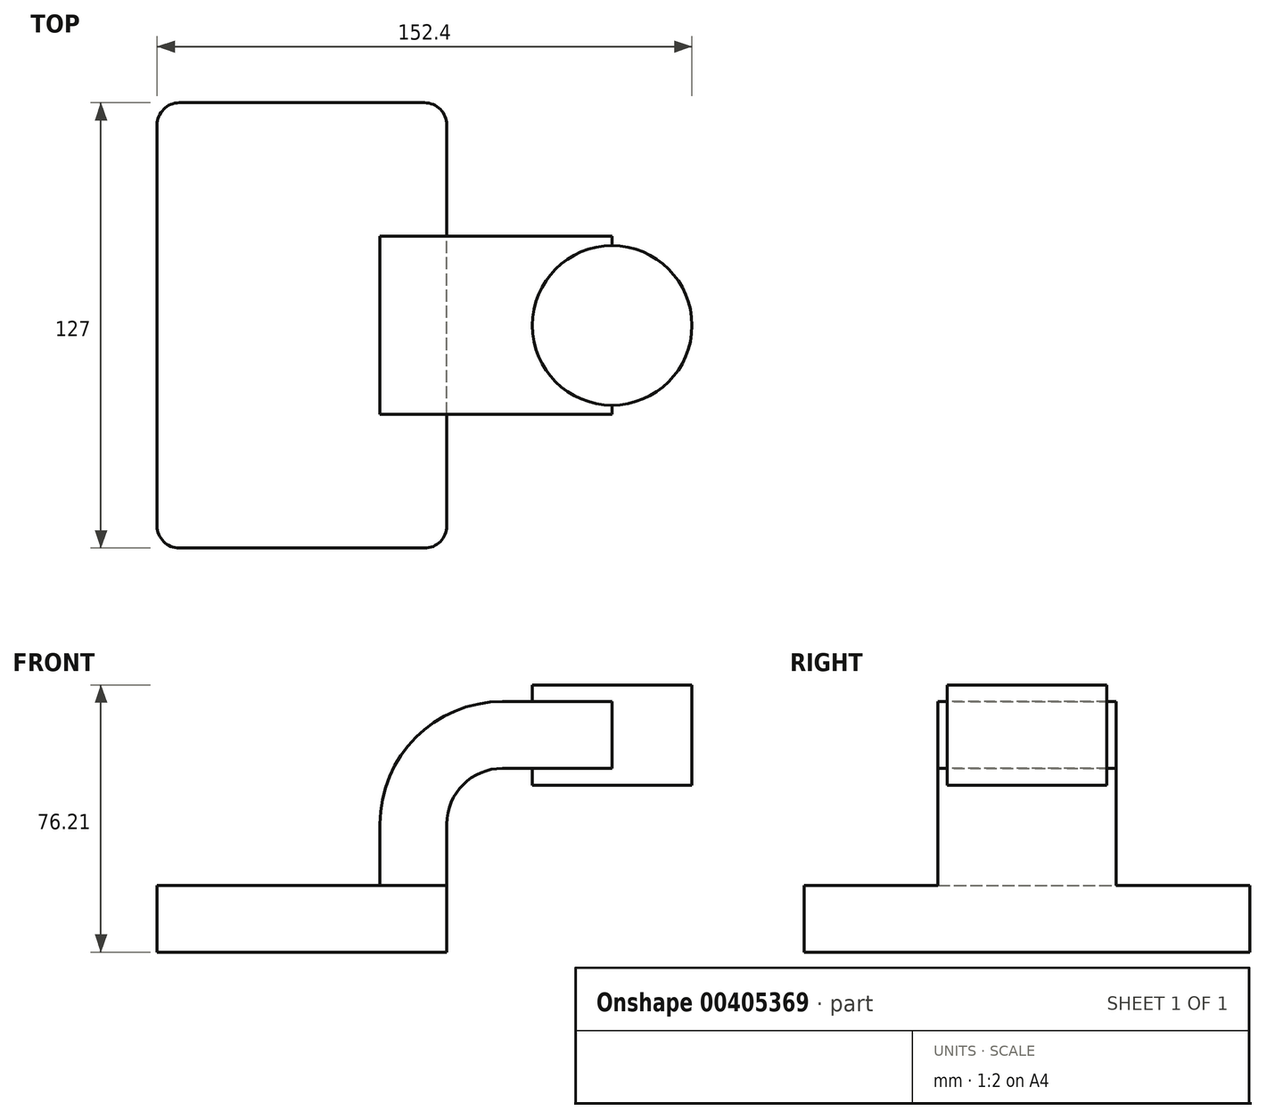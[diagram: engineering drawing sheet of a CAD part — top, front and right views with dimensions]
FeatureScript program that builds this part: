
annotation { "Feature Type Name" : "Feature", "Feature Type Description" : "" }
export const myFeature = defineFeature(function(context is Context, id is Id, definition is map)
    precondition{}
    {
        {
            var Q0;
            Q0=qCreatedBy(makeId("Front.planeOp"),FACE);
            var sketch = newSketch(context, id + "F0", { "sketchPlane" : qUnion([Q0])});
            skLineSegment(sketch, "E0.bottom", {"start": v(41.28, -9.52) * mm, "end": v(-41.28, -9.52) * mm});
            skLineSegment(sketch, "E0.top", {"start": v(41.28, 9.53) * mm, "end": v(-41.28, 9.53) * mm});
            skLineSegment(sketch, "E0.left", {"start": v(41.28, -9.52) * mm, "end": v(41.28, 9.53) * mm});
            skLineSegment(sketch, "E0.right", {"start": v(-41.28, -9.52) * mm, "end": v(-41.28, 9.53) * mm});
            skPoint(sketch, "E0.middle", {"position": v(0, 0) * mm});
            skLineSegment(sketch, "E1.bottom", {"start": v(60.32, 66.68) * mm, "end": v(111.12, 66.68) * mm});
            skLineSegment(sketch, "E1.top", {"start": v(60.32, 38.1) * mm, "end": v(111.12, 38.1) * mm});
            skLineSegment(sketch, "E1.left", {"start": v(60.32, 66.68) * mm, "end": v(60.32, 38.1) * mm});
            skLineSegment(sketch, "E1.right", {"start": v(111.12, 66.68) * mm, "end": v(111.12, 38.1) * mm});
            skPoint(sketch, "E1.middle", {"position": v(85.72, 52.39) * mm});
            skLineSegment(sketch, "E2", {"start": v(41.28, 9.53) * mm, "end": v(41.28, 27) * mm});
            skArc(sketch, "E3", {"start": v(41.27, 27) * mm, "mid": v(45.92, 38.23) * mm, "end": v(57.15, 42.88) * mm});
            skLineSegment(sketch, "E4", {"start": v(57.15, 42.88) * mm, "end": v(88.38, 42.88) * mm});
            skLineSegment(sketch, "E5.0", {"start": v(57.15, 61.93) * mm, "end": v(88.38, 61.93) * mm});
            skArc(sketch, "E5.1", {"start": v(22.23, 27) * mm, "mid": v(32.45, 51.7) * mm, "end": v(57.15, 61.93) * mm});
            skLineSegment(sketch, "E5.2", {"start": v(22.22, 9.53) * mm, "end": v(22.22, 27) * mm});
            skLineSegment(sketch, "E6", {"start": v(88.38, 61.93) * mm, "end": v(88.38, 38.1) * mm});
            skPoint(sketch, "E6.endSnap0", {"position": v(85.72, 38.1) * mm});
            skLineSegment(sketch, "E7", {"start": v(88.38, 38.1) * mm, "end": v(88.38, 66.68) * mm});
            skFitSpline(sketch, "E8", {"points": [v(-41.28, 9.53) * mm, v(57.15, 61.93) * mm], "startDerivative": vector(0, 101.5) * mm, "endDerivative": vector(218.9, 0) * mm});
            skPoint(sketch, "E9", {"position": v(72.77, 61.93) * mm});
            skSolve(sketch);
        }
        {
            var Q0;
            Q0=makeQuery(id+"F0.imprint","IMPRINT",FACE,{"disambiguationData":[TD([[makeQuery(id+"F0.imprint","IMPRINT",EDGE,{"derivedFrom":sQuery(id+"F0.wireOp",EDGE,"E0.bottom")}),-1.0]])]});
            extrude(context, id + "F1", {"entities" : qUnion([Q0]), "endBound" : BoundingType.SYMMETRIC, "depth" : 127 * mm});
        }
        {
            var Q0;
            {var subQ1=sQuery(id+"F0.wireOp",EDGE,"E2");Q0=makeQuery(id+"F0.imprint","IMPRINT",FACE,{"disambiguationData":[TD([[makeQuery(id+"F0.imprint","IMPRINT",EDGE,{"derivedFrom":subQ1}),1.0]])]});}
            var Q1;
            {var subQ0=sQuery(id+"F0.wireOp",EDGE,"E5.0");var subQ1=sQuery(id+"F0.wireOp",EDGE,"E1.left");var subQ2=makeQuery(id+"F0.imprint","INTERSECT",VERTEX,{"derivedFrom":[subQ1,subQ0]});Q1=makeQuery(id+"F0.imprint","IMPRINT",FACE,{"disambiguationData":[TD([[makeQuery(id+"F0.imprint","IMPRINT",EDGE,{"disambiguationData":[TD([[subQ2,-1.0]])],"derivedFrom":subQ1}),1.0]])]});}
            extrude(context, id + "F2", {"entities" : qUnion([Q0, Q1]), "operationType" : NewBodyOperationType.ADD, "endBound" : BoundingType.SYMMETRIC, "depth" : 50.8 * mm});
        }
        {
            var Q0;
            Q0=makeQuery(id+"F0.imprint","IMPRINT",FACE,{"disambiguationData":[TD([[makeQuery(id+"F0.imprint","IMPRINT",EDGE,{"derivedFrom":sQuery(id+"F0.wireOp",EDGE,"E5.1")}),1.0]])]});
            extrude(context, id + "F3", {"entities" : qUnion([Q0]), "operationType" : NewBodyOperationType.ADD, "endBound" : BoundingType.SYMMETRIC, "depth" : 15.88 * mm});
        }
        {
            var Q0;
            {var subQ0=sQuery(id+"F0.wireOp",EDGE,"E1.right");Q0=makeQuery(id+"F0.imprint","IMPRINT",FACE,{"disambiguationData":[TD([[makeQuery(id+"F0.imprint","IMPRINT",EDGE,{"derivedFrom":subQ0}),-1.0]])]});}
            var Q1;
            Q1=sQuery(id+"F0.wireOp",EDGE,"E7");
            revolve(context, id + "F4", {"operationType" : NewBodyOperationType.ADD, "entities" : qUnion([Q0]), "axis" : qUnion([Q1]), "revolveType" : RevolveType.FULL});
        }
        {
            var Q0;
            Q0=makeQuery(id+"F1.opExtrude","CAP_EDGE",EDGE,{"disambiguationData":[OSD([sQuery(id+"F0.wireOp",EDGE,"E0.left")])],"isStart":false});
            var Q1;
            Q1=makeQuery(id+"F1.opExtrude","CAP_EDGE",EDGE,{"disambiguationData":[OSD([sQuery(id+"F0.wireOp",EDGE,"E0.right")])],"isStart":false});
            var Q2;
            Q2=makeQuery(id+"F1.opExtrude","CAP_EDGE",EDGE,{"disambiguationData":[OSD([sQuery(id+"F0.wireOp",EDGE,"E0.left")])],"isStart":true});
            var Q3;
            Q3=makeQuery(id+"F1.opExtrude","CAP_EDGE",EDGE,{"disambiguationData":[OSD([sQuery(id+"F0.wireOp",EDGE,"E0.right")])],"isStart":true});
            fillet(context, id + "F5", {"entities" : qUnion([Q0, Q1, Q2, Q3]), "radius" : 6.35 * mm, "tangentPropagation" : true, "allowEdgeOverflow" : false});
        }
    });
